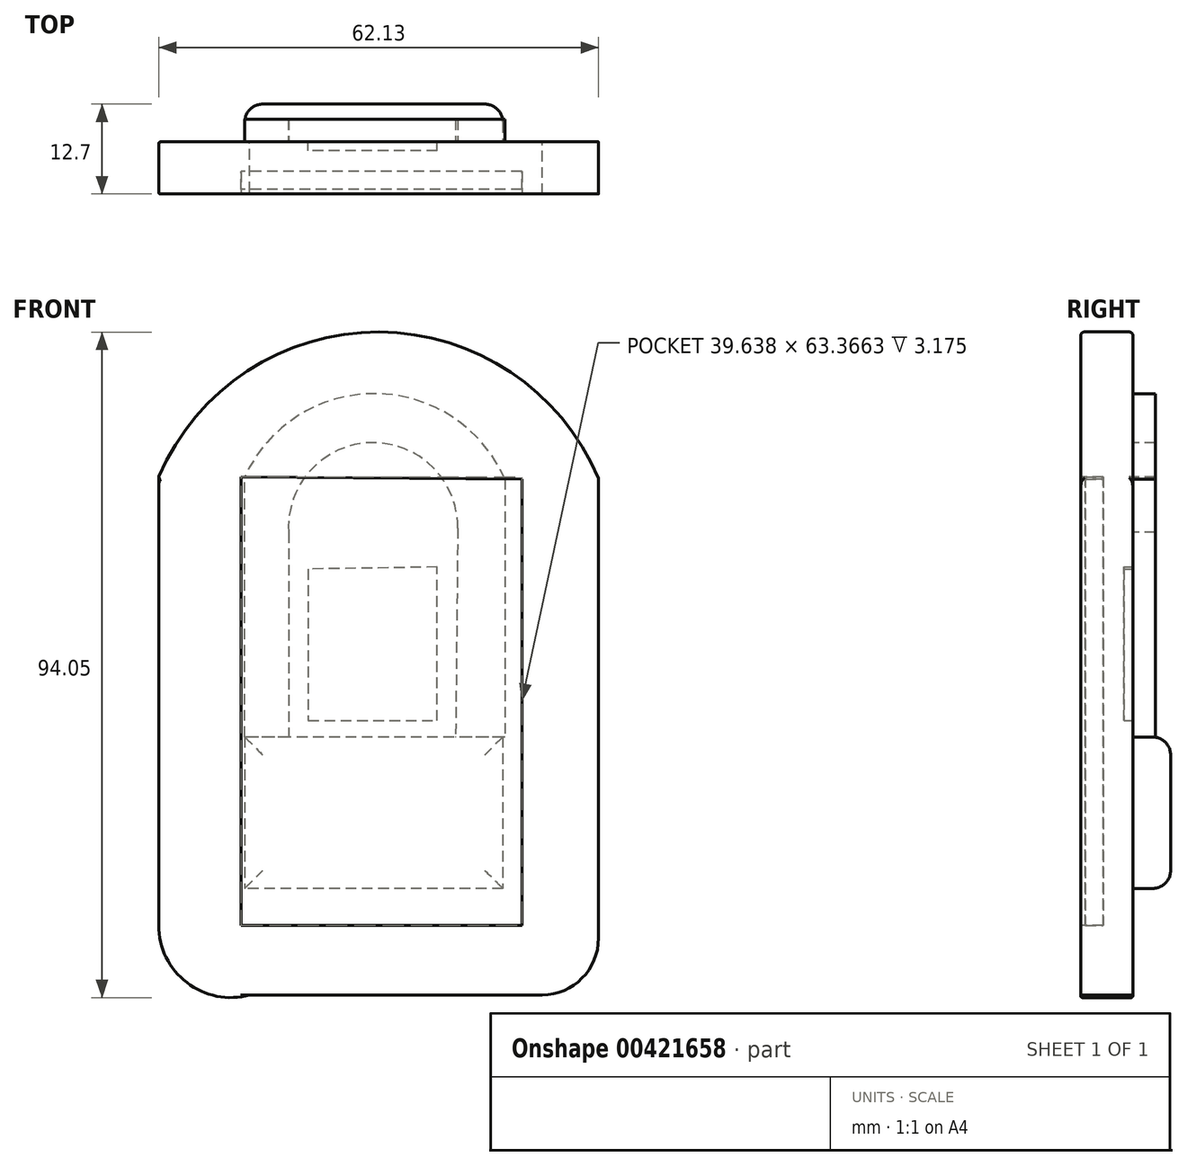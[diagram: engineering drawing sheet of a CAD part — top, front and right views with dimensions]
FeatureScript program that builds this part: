
annotation { "Feature Type Name" : "Feature", "Feature Type Description" : "" }
export const myFeature = defineFeature(function(context is Context, id is Id, definition is map)
    precondition{}
    {
        {
            var Q0;
            Q0=qCreatedBy(makeId("Front.planeOp"),FACE);
            var sketch = newSketch(context, id + "F0", { "sketchPlane" : qUnion([Q0])});
            skLineSegment(sketch, "E0", {"start": v(-74.67, -34.6) * mm, "end": v(-74.67, 28.76) * mm});
            skLineSegment(sketch, "E1", {"start": v(-12.54, -36.41) * mm, "end": v(-12.54, 28.47) * mm});
            skArc(sketch, "E2", {"start": v(-12.54, 28.47) * mm, "mid": v(-43.5, 49.24) * mm, "end": v(-74.67, 28.76) * mm});
            skArc(sketch, "E3", {"start": v(-74.67, -34.6) * mm, "mid": v(-70.67, -42.7) * mm, "end": v(-61.81, -44.46) * mm});
            skArc(sketch, "E4", {"start": v(-20.5, -44.46) * mm, "mid": v(-14.87, -42.07) * mm, "end": v(-12.54, -36.41) * mm});
            skLineSegment(sketch, "E5", {"start": v(-61.81, -44.46) * mm, "end": v(-20.5, -44.46) * mm});
            skSolve(sketch);
        }
        {
            var Q0;
            Q0=makeQuery(id+"F0.imprint","IMPRINT",FACE,{"disambiguationData":[TD([[makeQuery(id+"F0.imprint","IMPRINT",EDGE,{"derivedFrom":sQuery(id+"F0.wireOp",EDGE,"E0")}),-1.0]])]});
            extrude(context, id + "F1", {"entities" : qUnion([Q0]), "depth" : 7.37 * mm});
        }
        {
            var Q0;
            Q0=makeQuery(id+"F1.opExtrude","CAP_FACE",FACE,{"disambiguationData":[OSD([sQuery(id+"F0.wireOp",EDGE,"E0"),sQuery(id+"F0.wireOp",EDGE,"E1"),sQuery(id+"F0.wireOp",EDGE,"E2"),sQuery(id+"F0.wireOp",EDGE,"E3"),sQuery(id+"F0.wireOp",EDGE,"E4"),sQuery(id+"F0.wireOp",EDGE,"E5")])],"isStart":false});
            var sketch = newSketch(context, id + "F2", { "sketchPlane" : qUnion([Q0])});
            skLineSegment(sketch, "E6", {"start": v(-63, 28.76) * mm, "end": v(-63, -34.6) * mm});
            skLineSegment(sketch, "E7", {"start": v(-63, -34.6) * mm, "end": v(-23.37, -34.6) * mm});
            skLineSegment(sketch, "E8", {"start": v(-23.37, -34.6) * mm, "end": v(-23.37, 28.47) * mm});
            skLineSegment(sketch, "E9", {"start": v(-23.37, 28.47) * mm, "end": v(-63, 28.76) * mm});
            skSolve(sketch);
        }
        {
            var Q0;
            Q0=makeQuery(id+"F2.imprint","IMPRINT",FACE,{"disambiguationData":[TD([[makeQuery(id+"F2.imprint","IMPRINT",EDGE,{"derivedFrom":sQuery(id+"F2.wireOp",EDGE,"E6")}),1.0]])]});
            extrude(context, id + "F3", {"entities" : qUnion([Q0]), "operationType" : NewBodyOperationType.REMOVE, "oppositeDirection" : true, "depth" : 3.17 * mm});
        }
        {
            var Q0;
            Q0=makeQuery(id+"F3.boolean.opBoolean","COPY",FACE,{"derivedFrom":makeQuery(id+"F3.opExtrude","CAP_FACE",FACE,{"disambiguationData":[OSD([sQuery(id+"F2.wireOp",EDGE,"E6"),sQuery(id+"F2.wireOp",EDGE,"E7"),sQuery(id+"F2.wireOp",EDGE,"E8"),sQuery(id+"F2.wireOp",EDGE,"E9")])],"isStart":false})});
            extrude(context, id + "F4", {"entities" : qUnion([Q0]), "depth" : 2.54 * mm});
        }
        {
            var Q0;
            Q0=makeQuery(id+"F1.opExtrude","CAP_FACE",FACE,{"disambiguationData":[OSD([sQuery(id+"F0.wireOp",EDGE,"E0"),sQuery(id+"F0.wireOp",EDGE,"E1"),sQuery(id+"F0.wireOp",EDGE,"E2"),sQuery(id+"F0.wireOp",EDGE,"E3"),sQuery(id+"F0.wireOp",EDGE,"E4"),sQuery(id+"F0.wireOp",EDGE,"E5")])],"isStart":true});
            var sketch = newSketch(context, id + "F5", { "sketchPlane" : qUnion([Q0])});
            skArc(sketch, "E10", {"start": v(62.51, 28.76) * mm, "mid": v(44.05, 40.53) * mm, "end": v(25.77, 28.47) * mm});
            skLineSegment(sketch, "E11", {"start": v(25.77, -7.98) * mm, "end": v(62.51, -7.98) * mm});
            skArc(sketch, "E12", {"start": v(56.31, 20.94) * mm, "mid": v(44.67, 33.6) * mm, "end": v(32.42, 21.53) * mm});
            skLineSegment(sketch, "E13", {"start": v(32.42, 21.53) * mm, "end": v(32.71, -7.98) * mm});
            skLineSegment(sketch, "E14", {"start": v(56.31, 20.94) * mm, "end": v(56.31, -7.98) * mm});
            skLineSegment(sketch, "E15", {"start": v(25.77, 28.47) * mm, "end": v(25.77, -7.98) * mm});
            skLineSegment(sketch, "E16", {"start": v(62.51, -7.98) * mm, "end": v(62.51, 28.76) * mm});
            skSolve(sketch);
        }
        {
            var Q0;
            {var subQ4=sQuery(id+"F5.wireOp",EDGE,"E10");Q0=makeQuery(id+"F5.imprint","IMPRINT",FACE,{"disambiguationData":[TD([[makeQuery(id+"F5.imprint","IMPRINT",EDGE,{"derivedFrom":subQ4}),1.0]])]});}
            var Q1;
            {var subQ5=sQuery(id+"F5.wireOp",EDGE,"OCNvw9NC-Goyg-xHDv-wVzX-tuvNvPi5UqDr");Q1=makeQuery(id+"F5.imprint","IMPRINT",FACE,{"disambiguationData":[TD([[makeQuery(id+"F5.imprint","IMPRINT",EDGE,{"derivedFrom":subQ5}),1.0]])]});}
            extrude(context, id + "F6", {"entities" : qUnion([Q0, Q1]), "depth" : 3.17 * mm});
        }
        {
            var Q0;
            Q0=makeQuery(id+"F1.opExtrude","CAP_FACE",FACE,{"disambiguationData":[OSD([sQuery(id+"F0.wireOp",EDGE,"E0"),sQuery(id+"F0.wireOp",EDGE,"E1"),sQuery(id+"F0.wireOp",EDGE,"E2"),sQuery(id+"F0.wireOp",EDGE,"E3"),sQuery(id+"F0.wireOp",EDGE,"E4"),sQuery(id+"F0.wireOp",EDGE,"E5")])],"isStart":true});
            var sketch = newSketch(context, id + "F7", { "sketchPlane" : qUnion([Q0])});
            skLineSegment(sketch, "E17.bottom", {"start": v(26.06, -7.98) * mm, "end": v(62.51, -7.98) * mm});
            skLineSegment(sketch, "E17.top", {"start": v(26.06, -29.4) * mm, "end": v(62.51, -29.4) * mm});
            skLineSegment(sketch, "E17.left", {"start": v(26.06, -7.98) * mm, "end": v(26.06, -29.4) * mm});
            skLineSegment(sketch, "E17.right", {"start": v(62.51, -7.98) * mm, "end": v(62.51, -29.4) * mm});
            skSolve(sketch);
        }
        {
            var Q0;
            Q0=makeQuery(id+"F7.imprint","IMPRINT",FACE,{"disambiguationData":[TD([[makeQuery(id+"F7.imprint","IMPRINT",EDGE,{"derivedFrom":sQuery(id+"F7.wireOp",EDGE,"E17.bottom")}),-1.0]])]});
            extrude(context, id + "F8", {"entities" : qUnion([Q0]), "depth" : 5.33 * mm});
        }
        {
            var Q0;
            Q0=makeQuery(id+"F8.opExtrude","CAP_FACE",FACE,{"disambiguationData":[OSD([sQuery(id+"F7.wireOp",EDGE,"E17.bottom"),sQuery(id+"F7.wireOp",EDGE,"E17.top"),sQuery(id+"F7.wireOp",EDGE,"E17.left"),sQuery(id+"F7.wireOp",EDGE,"E17.right")])],"isStart":false});
            fillet(context, id + "F9", {"entities" : qUnion([Q0]), "radius" : 2.54 * mm, "tangentPropagation" : true, "allowEdgeOverflow" : false});
        }
        {
            var Q0;
            Q0=makeQuery(id+"F1.opExtrude","CAP_FACE",FACE,{"disambiguationData":[OSD([sQuery(id+"F0.wireOp",EDGE,"E0"),sQuery(id+"F0.wireOp",EDGE,"E1"),sQuery(id+"F0.wireOp",EDGE,"E2"),sQuery(id+"F0.wireOp",EDGE,"E3"),sQuery(id+"F0.wireOp",EDGE,"E4"),sQuery(id+"F0.wireOp",EDGE,"E5")])],"isStart":true});
            var sketch = newSketch(context, id + "F10", { "sketchPlane" : qUnion([Q0])});
            skLineSegment(sketch, "E18", {"start": v(53.54, 15.74) * mm, "end": v(53.54, -5.67) * mm});
            skLineSegment(sketch, "E19", {"start": v(53.54, -5.67) * mm, "end": v(35.32, -5.67) * mm});
            skLineSegment(sketch, "E20", {"start": v(35.32, -5.67) * mm, "end": v(35.32, 16.03) * mm});
            skLineSegment(sketch, "E21", {"start": v(35.32, 16.03) * mm, "end": v(53.54, 15.74) * mm});
            skSolve(sketch);
        }
        {
            var Q0;
            Q0=makeQuery(id+"F10.imprint","IMPRINT",FACE,{"disambiguationData":[TD([[makeQuery(id+"F10.imprint","IMPRINT",EDGE,{"derivedFrom":sQuery(id+"F10.wireOp",EDGE,"E18")}),-1.0]])]});
            extrude(context, id + "F11", {"entities" : qUnion([Q0]), "oppositeDirection" : true, "depth" : 1.27 * mm});
        }
        {
            var Q0;
            Q0=makeQuery(id+"F1.opExtrude","SWEPT_FACE",FACE,{"disambiguationData":[OSD([sQuery(id+"F0.wireOp",EDGE,"E2")])]});
            fillet(context, id + "F12", {"entities" : qUnion([Q0]), "radius" : 0.48 * mm, "tangentPropagation" : true, "allowEdgeOverflow" : false});
        }
        {
            var Q0;
            Q0=makeQuery(id+"F1.opExtrude","SWEPT_FACE",FACE,{"disambiguationData":[OSD([sQuery(id+"F0.wireOp",EDGE,"E0")])]});
            fillet(context, id + "F13", {"entities" : qUnion([Q0]), "radius" : 0.25 * mm, "tangentPropagation" : true, "allowEdgeOverflow" : false});
        }
    });
